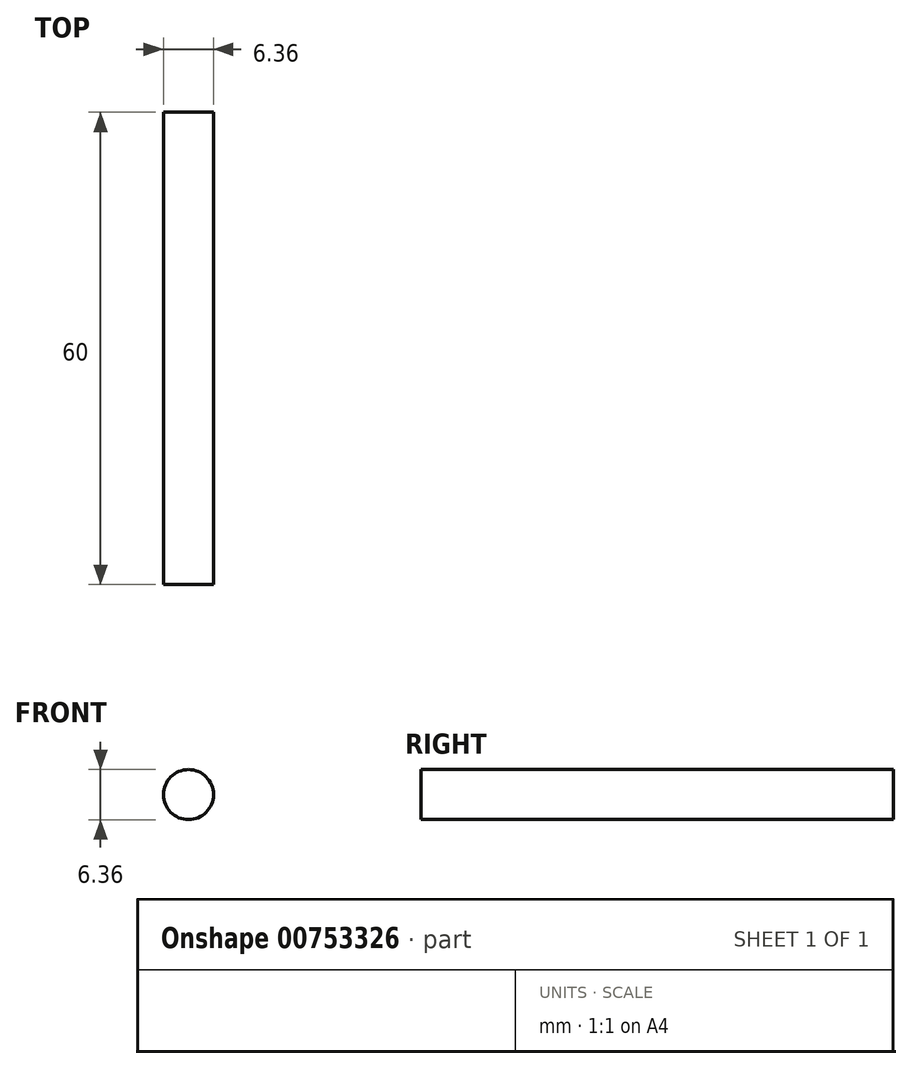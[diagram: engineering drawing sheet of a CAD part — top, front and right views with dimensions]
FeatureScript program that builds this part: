
annotation { "Feature Type Name" : "Feature", "Feature Type Description" : "" }
export const myFeature = defineFeature(function(context is Context, id is Id, definition is map)
    precondition{}
    {
        {
            var Q0;
            Q0=qCreatedBy(makeId("Front.planeOp"),FACE);
            var sketch = newSketch(context, id + "F0", { "sketchPlane" : qUnion([Q0])});
            skCircle(sketch, "E0", {"center": v(0, 0) * mm, "radius": 3.18 * mm});
            skSolve(sketch);
        }
        {
            var Q0;
            Q0=makeQuery(id+"F0.imprint","IMPRINT",FACE,{"disambiguationData":[TD([[makeQuery(id+"F0.imprint","IMPRINT",EDGE,{"derivedFrom":sQuery(id+"F0.wireOp",EDGE,"E0")}),1.0]])]});
            extrude(context, id + "F1", {"entities" : qUnion([Q0]), "depth" : 60 * mm, "offsetDistance" : 25.4 * mm});
        }
    });
